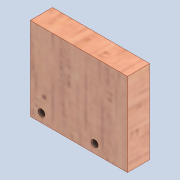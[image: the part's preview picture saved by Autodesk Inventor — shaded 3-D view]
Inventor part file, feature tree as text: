
AUTODESK INVENTOR PART (.ipt)
format: ipt  version: 2020 (Build 240168000, 168)  size: 131,072 bytes
history: native  units: mm
features: other x3, sketch x2, reference x2, extrude x1, hole x1
ambient origin geometry x8: Origin, YZ Plane, XZ Plane, XY Plane, X Axis, Y Axis, Z Axis, Center Point
bodies: Solid1 (feature_tree)
feature tree (9):
  extrude  "Extrusion1"  Depth=30.0mm
  hole  "Hole1"  [1 undecoded]
  sketch  "Sketch1"  dims[d0=35.0mm d1=30.0mm]
  sketch  "Sketch6"  dims[d2=8.0mm d3=0.0mm d37=2.459mm d38=8.0mm d39=4.0mm d40=2.0mm d41=90.0deg d42=8.8mm d43=20.594885mm]
  reference  "Reference1"
  reference  "Reference2"
  parser-record x1  (decoder bookkeeping rows leaked as tree rows — omitted from the tree; the rows remain in map.json)
  other  "0005-00-00 Ansamblu_General_V1.iam"
  other  "0005-20-1003 Switch:1"
note: 1 required parameter value undecoded (feature->parameter linkage not recoverable at this tier; creation-order binding heuristic only, values carry confidence <= 0.55)
note: 1 file-system path scrubbed to <path> (originals preserved in map.json)
